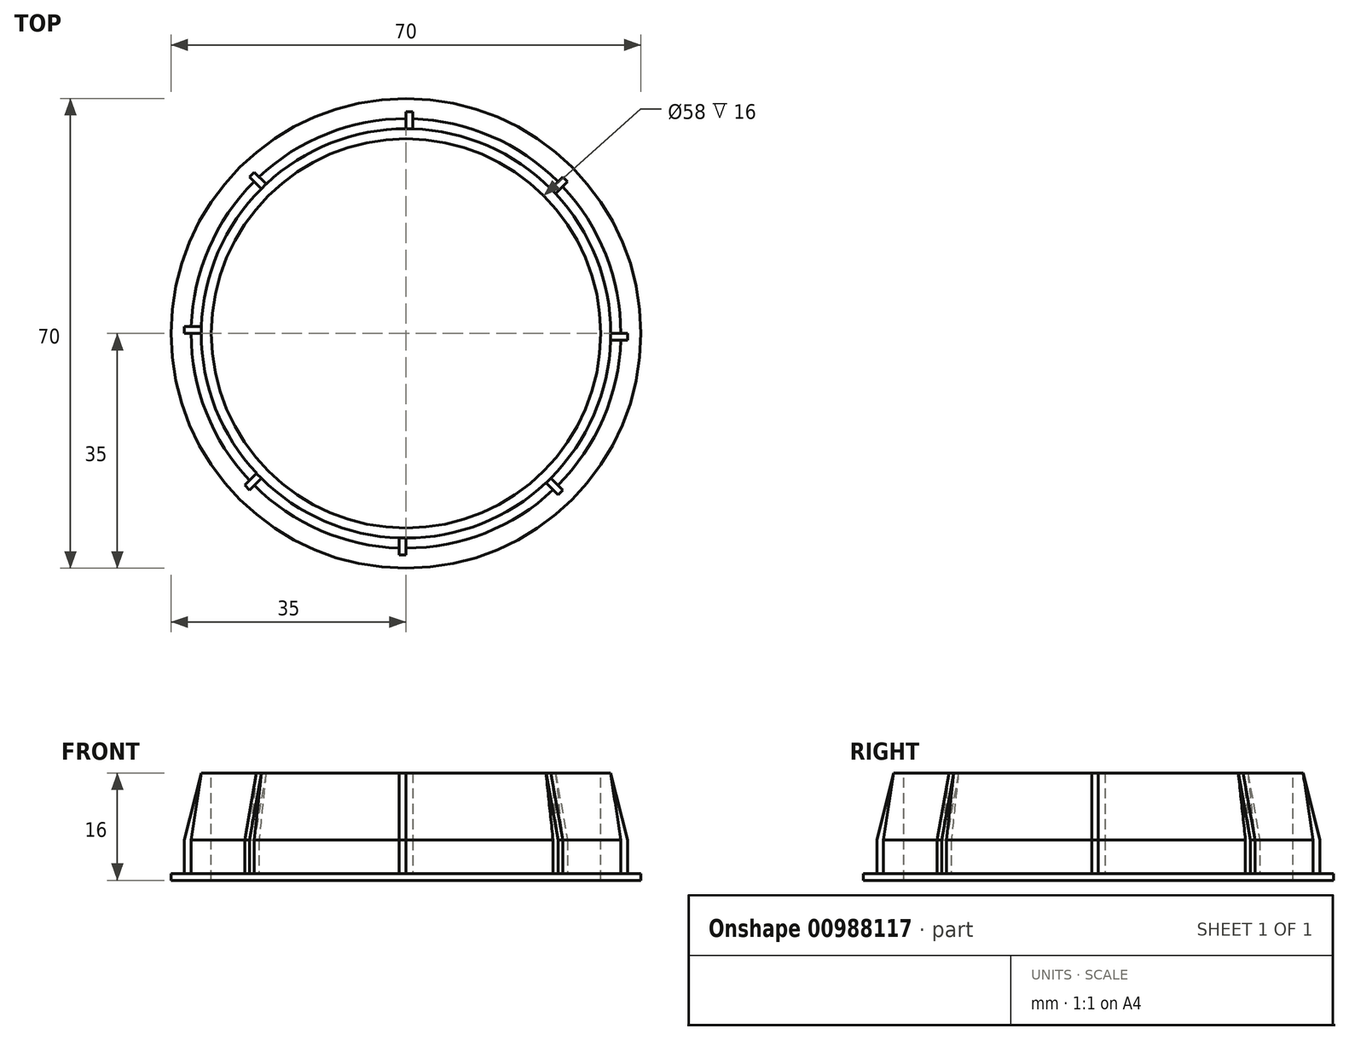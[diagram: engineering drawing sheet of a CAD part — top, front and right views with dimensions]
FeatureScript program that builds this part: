
annotation { "Feature Type Name" : "Feature", "Feature Type Description" : "" }
export const myFeature = defineFeature(function(context is Context, id is Id, definition is map)
    precondition{}
    {
        {
            var Q0;
            Q0=qCreatedBy(makeId("Top.planeOp"),FACE);
            var sketch = newSketch(context, id + "F0", { "sketchPlane" : qUnion([Q0])});
            skCircle(sketch, "E0", {"center": v(0, 0) * mm, "radius": 35 * mm});
            skSolve(sketch);
        }
        {
            var Q0;
            Q0 = qSketchRegion(id + "F0", true);
            extrude(context, id + "F1", {"entities" : qUnion([Q0]), "depth" : 1 * mm, "offsetDistance" : 25 * mm});
        }
        {
            var Q0;
            Q0=makeQuery(id+"F1.opExtrude","CAP_FACE",FACE,{"disambiguationData":[OSD([sQuery(id+"F0.wireOp",EDGE,"E0")])],"isStart":false});
            var sketch = newSketch(context, id + "F2", { "sketchPlane" : qUnion([Q0])});
            skCircle(sketch, "E1", {"center": v(0, 0) * mm, "radius": 32 * mm});
            skLineSegment(sketch, "E2.bottom", {"start": v(0, 32) * mm, "end": v(1, 32) * mm});
            skLineSegment(sketch, "E2.top", {"start": v(0, 33) * mm, "end": v(1, 33) * mm});
            skLineSegment(sketch, "E2.left", {"start": v(0, 32) * mm, "end": v(0, 33) * mm});
            skLineSegment(sketch, "E2.right", {"start": v(1, 32) * mm, "end": v(1, 33) * mm});
            skLineSegment(sketch, "E3.top", {"start": v(0, 31) * mm, "end": v(1, 31) * mm});
            skLineSegment(sketch, "E3.left", {"start": v(0, 32) * mm, "end": v(0, 31) * mm});
            skLineSegment(sketch, "E3.right", {"start": v(1, 32) * mm, "end": v(1, 31) * mm});
            skLineSegment(sketch, "E4.1.0", {"start": v(-22.63, 22.63) * mm, "end": v(-23.33, 23.33) * mm});
            skLineSegment(sketch, "E4.1.1", {"start": v(-21.92, 23.33) * mm, "end": v(-21.21, 22.63) * mm});
            skLineSegment(sketch, "E4.1.2", {"start": v(-22.63, 22.63) * mm, "end": v(-21.92, 21.92) * mm});
            skLineSegment(sketch, "E4.1.3", {"start": v(-23.33, 23.33) * mm, "end": v(-22.63, 24.04) * mm});
            skLineSegment(sketch, "E4.1.4", {"start": v(-21.92, 23.33) * mm, "end": v(-22.63, 24.04) * mm});
            skLineSegment(sketch, "E4.1.5", {"start": v(-22.63, 22.63) * mm, "end": v(-21.92, 23.33) * mm});
            skLineSegment(sketch, "E4.1.6", {"start": v(-21.92, 21.92) * mm, "end": v(-21.21, 22.63) * mm});
            skLineSegment(sketch, "E4.1.7", {"start": v(-22.63, 22.63) * mm, "end": v(-21.92, 23.33) * mm});
            skLineSegment(sketch, "E4.2.0", {"start": v(-32, 0) * mm, "end": v(-33, 0) * mm});
            skLineSegment(sketch, "E4.2.1", {"start": v(-32, 1) * mm, "end": v(-31, 1) * mm});
            skLineSegment(sketch, "E4.2.2", {"start": v(-32, 0) * mm, "end": v(-31, 0) * mm});
            skLineSegment(sketch, "E4.2.3", {"start": v(-33, 0) * mm, "end": v(-33, 1) * mm});
            skLineSegment(sketch, "E4.2.4", {"start": v(-32, 1) * mm, "end": v(-33, 1) * mm});
            skLineSegment(sketch, "E4.2.5", {"start": v(-32, 0) * mm, "end": v(-32, 1) * mm});
            skLineSegment(sketch, "E4.2.6", {"start": v(-31, 0) * mm, "end": v(-31, 1) * mm});
            skLineSegment(sketch, "E4.2.7", {"start": v(-32, 0) * mm, "end": v(-32, 1) * mm});
            skLineSegment(sketch, "E4.3.0", {"start": v(-22.63, -22.63) * mm, "end": v(-23.33, -23.33) * mm});
            skLineSegment(sketch, "E4.3.1", {"start": v(-23.33, -21.92) * mm, "end": v(-22.63, -21.21) * mm});
            skLineSegment(sketch, "E4.3.2", {"start": v(-22.63, -22.63) * mm, "end": v(-21.92, -21.92) * mm});
            skLineSegment(sketch, "E4.3.3", {"start": v(-23.33, -23.33) * mm, "end": v(-24.04, -22.63) * mm});
            skLineSegment(sketch, "E4.3.4", {"start": v(-23.33, -21.92) * mm, "end": v(-24.04, -22.63) * mm});
            skLineSegment(sketch, "E4.3.5", {"start": v(-22.63, -22.63) * mm, "end": v(-23.33, -21.92) * mm});
            skLineSegment(sketch, "E4.3.6", {"start": v(-21.92, -21.92) * mm, "end": v(-22.63, -21.21) * mm});
            skLineSegment(sketch, "E4.3.7", {"start": v(-22.63, -22.63) * mm, "end": v(-23.33, -21.92) * mm});
            skLineSegment(sketch, "E4.4.0", {"start": v(0, -32) * mm, "end": v(0, -33) * mm});
            skLineSegment(sketch, "E4.4.1", {"start": v(-1, -32) * mm, "end": v(-1, -31) * mm});
            skLineSegment(sketch, "E4.4.2", {"start": v(0, -32) * mm, "end": v(0, -31) * mm});
            skLineSegment(sketch, "E4.4.3", {"start": v(0, -33) * mm, "end": v(-1, -33) * mm});
            skLineSegment(sketch, "E4.4.4", {"start": v(-1, -32) * mm, "end": v(-1, -33) * mm});
            skLineSegment(sketch, "E4.4.5", {"start": v(0, -32) * mm, "end": v(-1, -32) * mm});
            skLineSegment(sketch, "E4.4.6", {"start": v(0, -31) * mm, "end": v(-1, -31) * mm});
            skLineSegment(sketch, "E4.4.7", {"start": v(0, -32) * mm, "end": v(-1, -32) * mm});
            skLineSegment(sketch, "E4.5.0", {"start": v(22.63, -22.63) * mm, "end": v(23.33, -23.33) * mm});
            skLineSegment(sketch, "E4.5.1", {"start": v(21.92, -23.33) * mm, "end": v(21.21, -22.63) * mm});
            skLineSegment(sketch, "E4.5.2", {"start": v(22.63, -22.63) * mm, "end": v(21.92, -21.92) * mm});
            skLineSegment(sketch, "E4.5.3", {"start": v(23.33, -23.33) * mm, "end": v(22.63, -24.04) * mm});
            skLineSegment(sketch, "E4.5.4", {"start": v(21.92, -23.33) * mm, "end": v(22.63, -24.04) * mm});
            skLineSegment(sketch, "E4.5.5", {"start": v(22.63, -22.63) * mm, "end": v(21.92, -23.33) * mm});
            skLineSegment(sketch, "E4.5.6", {"start": v(21.92, -21.92) * mm, "end": v(21.21, -22.63) * mm});
            skLineSegment(sketch, "E4.5.7", {"start": v(22.63, -22.63) * mm, "end": v(21.92, -23.33) * mm});
            skLineSegment(sketch, "E4.6.0", {"start": v(32, 0) * mm, "end": v(33, 0) * mm});
            skLineSegment(sketch, "E4.6.1", {"start": v(32, -1) * mm, "end": v(31, -1) * mm});
            skLineSegment(sketch, "E4.6.2", {"start": v(32, 0) * mm, "end": v(31, 0) * mm});
            skLineSegment(sketch, "E4.6.3", {"start": v(33, 0) * mm, "end": v(33, -1) * mm});
            skLineSegment(sketch, "E4.6.4", {"start": v(32, -1) * mm, "end": v(33, -1) * mm});
            skLineSegment(sketch, "E4.6.5", {"start": v(32, 0) * mm, "end": v(32, -1) * mm});
            skLineSegment(sketch, "E4.6.6", {"start": v(31, 0) * mm, "end": v(31, -1) * mm});
            skLineSegment(sketch, "E4.6.7", {"start": v(32, 0) * mm, "end": v(32, -1) * mm});
            skLineSegment(sketch, "E4.7.0", {"start": v(22.63, 22.63) * mm, "end": v(23.33, 23.33) * mm});
            skLineSegment(sketch, "E4.7.1", {"start": v(23.33, 21.92) * mm, "end": v(22.63, 21.21) * mm});
            skLineSegment(sketch, "E4.7.2", {"start": v(22.63, 22.63) * mm, "end": v(21.92, 21.92) * mm});
            skLineSegment(sketch, "E4.7.3", {"start": v(23.33, 23.33) * mm, "end": v(24.04, 22.63) * mm});
            skLineSegment(sketch, "E4.7.4", {"start": v(23.33, 21.92) * mm, "end": v(24.04, 22.63) * mm});
            skLineSegment(sketch, "E4.7.5", {"start": v(22.63, 22.63) * mm, "end": v(23.33, 21.92) * mm});
            skLineSegment(sketch, "E4.7.6", {"start": v(21.92, 21.92) * mm, "end": v(22.63, 21.21) * mm});
            skLineSegment(sketch, "E4.7.7", {"start": v(22.63, 22.63) * mm, "end": v(23.33, 21.92) * mm});
            skSolve(sketch);
        }
        {
            var Q0;
            Q0 = qSketchRegion(id + "F2", true);
            extrude(context, id + "F3", {"entities" : qUnion([Q0]), "operationType" : NewBodyOperationType.ADD, "depth" : 15 * mm, "offsetDistance" : 25 * mm});
        }
        {
            var Q0;
            Q0=makeQuery(id+"F3.opExtrude","CAP_FACE",FACE,{"disambiguationData":[OSD([sQuery(id+"F2.wireOp",EDGE,"E1"),sQuery(id+"F2.wireOp",EDGE,"E2.top"),sQuery(id+"F2.wireOp",EDGE,"E2.left"),sQuery(id+"F2.wireOp",EDGE,"E2.right"),sQuery(id+"F2.wireOp",EDGE,"E3.right"),sQuery(id+"F2.wireOp",EDGE,"E4.1.0"),sQuery(id+"F2.wireOp",EDGE,"E4.1.1"),sQuery(id+"F2.wireOp",EDGE,"E4.1.3"),sQuery(id+"F2.wireOp",EDGE,"E4.1.4"),sQuery(id+"F2.wireOp",EDGE,"E4.2.0"),sQuery(id+"F2.wireOp",EDGE,"E4.2.1"),sQuery(id+"F2.wireOp",EDGE,"E4.2.3"),sQuery(id+"F2.wireOp",EDGE,"E4.2.4"),sQuery(id+"F2.wireOp",EDGE,"E4.3.0"),sQuery(id+"F2.wireOp",EDGE,"E4.3.1"),sQuery(id+"F2.wireOp",EDGE,"E4.3.3"),sQuery(id+"F2.wireOp",EDGE,"E4.3.4"),sQuery(id+"F2.wireOp",EDGE,"E4.4.0"),sQuery(id+"F2.wireOp",EDGE,"E4.4.1"),sQuery(id+"F2.wireOp",EDGE,"E4.4.3"),sQuery(id+"F2.wireOp",EDGE,"E4.4.4"),sQuery(id+"F2.wireOp",EDGE,"E4.5.0"),sQuery(id+"F2.wireOp",EDGE,"E4.5.1"),sQuery(id+"F2.wireOp",EDGE,"E4.5.3"),sQuery(id+"F2.wireOp",EDGE,"E4.5.4"),sQuery(id+"F2.wireOp",EDGE,"E4.6.0"),sQuery(id+"F2.wireOp",EDGE,"E4.6.1"),sQuery(id+"F2.wireOp",EDGE,"E4.6.3"),sQuery(id+"F2.wireOp",EDGE,"E4.6.4"),sQuery(id+"F2.wireOp",EDGE,"E4.7.0"),sQuery(id+"F2.wireOp",EDGE,"E4.7.1"),sQuery(id+"F2.wireOp",EDGE,"E4.7.3"),sQuery(id+"F2.wireOp",EDGE,"E4.7.4")])],"isStart":false});
            var sketch = newSketch(context, id + "F4", { "sketchPlane" : qUnion([Q0])});
            skCircle(sketch, "E5", {"center": v(0, 0) * mm, "radius": 29 * mm});
            skSolve(sketch);
        }
        {
            var Q0;
            Q0 = qSketchRegion(id + "F4", true);
            extrude(context, id + "F5", {"entities" : qUnion([Q0]), "operationType" : NewBodyOperationType.REMOVE, "endBound" : BoundingType.THROUGH_ALL, "oppositeDirection" : true, "depth" : 25 * mm, "offsetDistance" : 25 * mm});
        }
        {
            var Q0;
            {var subQ0=sQuery(id+"F2.wireOp",EDGE,"E1");Q0=makeQuery(id+"F3.opExtrude","CAP_EDGE",EDGE,{"disambiguationData":[OSD([subQ0]),TDD([makeQuery(id+"F2.imprint","IMPRINT",EDGE,{"disambiguationData":[TD([[makeQuery(id+"F2.imprint","INTERSECT",VERTEX,{"derivedFrom":[subQ0,sQuery(id+"F2.wireOp",EDGE,"E3.right")]}),1.0]])],"derivedFrom":subQ0})])],"isStart":false});}
            var Q1;
            {var subQ0=sQuery(id+"F2.wireOp",EDGE,"E1");Q1=makeQuery(id+"F3.opExtrude","CAP_EDGE",EDGE,{"disambiguationData":[OSD([subQ0]),TDD([makeQuery(id+"F2.imprint","IMPRINT",EDGE,{"disambiguationData":[TD([[makeQuery(id+"F2.imprint","INTERSECT",VERTEX,{"derivedFrom":[subQ0,sQuery(id+"F2.wireOp",EDGE,"E4.7.1")]}),1.0]])],"derivedFrom":subQ0})])],"isStart":false});}
            var Q2;
            {var subQ0=sQuery(id+"F2.wireOp",EDGE,"E1");Q2=makeQuery(id+"F3.opExtrude","CAP_EDGE",EDGE,{"disambiguationData":[OSD([subQ0]),TDD([makeQuery(id+"F2.imprint","IMPRINT",EDGE,{"disambiguationData":[TD([[makeQuery(id+"F2.imprint","INTERSECT",VERTEX,{"derivedFrom":[subQ0,sQuery(id+"F2.wireOp",EDGE,"E4.6.1")]}),1.0]])],"derivedFrom":subQ0})])],"isStart":false});}
            var Q3;
            {var subQ0=sQuery(id+"F2.wireOp",EDGE,"E1");Q3=makeQuery(id+"F3.opExtrude","CAP_EDGE",EDGE,{"disambiguationData":[OSD([subQ0]),TDD([makeQuery(id+"F2.imprint","IMPRINT",EDGE,{"disambiguationData":[TD([[makeQuery(id+"F2.imprint","INTERSECT",VERTEX,{"derivedFrom":[subQ0,sQuery(id+"F2.wireOp",EDGE,"E4.5.1")]}),1.0]])],"derivedFrom":subQ0})])],"isStart":false});}
            var Q4;
            {var subQ0=sQuery(id+"F2.wireOp",EDGE,"E1");Q4=makeQuery(id+"F3.opExtrude","CAP_EDGE",EDGE,{"disambiguationData":[OSD([subQ0]),TDD([makeQuery(id+"F2.imprint","IMPRINT",EDGE,{"disambiguationData":[TD([[makeQuery(id+"F2.imprint","INTERSECT",VERTEX,{"derivedFrom":[subQ0,sQuery(id+"F2.wireOp",EDGE,"E4.4.1")]}),1.0]])],"derivedFrom":subQ0})])],"isStart":false});}
            var Q5;
            {var subQ0=sQuery(id+"F2.wireOp",EDGE,"E1");Q5=makeQuery(id+"F3.opExtrude","CAP_EDGE",EDGE,{"disambiguationData":[OSD([subQ0]),TDD([makeQuery(id+"F2.imprint","IMPRINT",EDGE,{"disambiguationData":[TD([[makeQuery(id+"F2.imprint","INTERSECT",VERTEX,{"derivedFrom":[subQ0,sQuery(id+"F2.wireOp",EDGE,"E4.3.1")]}),1.0]])],"derivedFrom":subQ0})])],"isStart":false});}
            var Q6;
            {var subQ0=sQuery(id+"F2.wireOp",EDGE,"E1");Q6=makeQuery(id+"F3.opExtrude","CAP_EDGE",EDGE,{"disambiguationData":[OSD([subQ0]),TDD([makeQuery(id+"F2.imprint","IMPRINT",EDGE,{"disambiguationData":[TD([[makeQuery(id+"F2.imprint","INTERSECT",VERTEX,{"derivedFrom":[subQ0,sQuery(id+"F2.wireOp",EDGE,"E4.2.1")]}),1.0]])],"derivedFrom":subQ0})])],"isStart":false});}
            var Q7;
            {var subQ0=sQuery(id+"F2.wireOp",EDGE,"E1");Q7=makeQuery(id+"F3.opExtrude","CAP_EDGE",EDGE,{"disambiguationData":[OSD([subQ0]),TDD([makeQuery(id+"F2.imprint","IMPRINT",EDGE,{"disambiguationData":[TD([[makeQuery(id+"F2.imprint","INTERSECT",VERTEX,{"derivedFrom":[subQ0,sQuery(id+"F2.wireOp",EDGE,"E4.1.1")]}),1.0]])],"derivedFrom":subQ0})])],"isStart":false});}
            chamfer(context, id + "F6", {"entities" : qUnion([Q0, Q1, Q2, Q3, Q4, Q5, Q6, Q7]), "chamferType" : ChamferType.TWO_OFFSETS, "width1" : 1.5 * mm, "oppositeDirection" : false, "width2" : 10 * mm, "tangentPropagation" : true});
        }
        {
            var Q0;
            Q0=makeQuery(id+"F3.opExtrude","CAP_EDGE",EDGE,{"disambiguationData":[OSD([sQuery(id+"F2.wireOp",EDGE,"E4.6.3")])],"isStart":false});
            var Q1;
            Q1=makeQuery(id+"F3.opExtrude","CAP_EDGE",EDGE,{"disambiguationData":[OSD([sQuery(id+"F2.wireOp",EDGE,"E4.5.3")])],"isStart":false});
            var Q2;
            Q2=makeQuery(id+"F3.opExtrude","CAP_EDGE",EDGE,{"disambiguationData":[OSD([sQuery(id+"F2.wireOp",EDGE,"E4.4.3")])],"isStart":false});
            var Q3;
            Q3=makeQuery(id+"F3.opExtrude","CAP_EDGE",EDGE,{"disambiguationData":[OSD([sQuery(id+"F2.wireOp",EDGE,"E4.3.3")])],"isStart":false});
            var Q4;
            Q4=makeQuery(id+"F3.opExtrude","CAP_EDGE",EDGE,{"disambiguationData":[OSD([sQuery(id+"F2.wireOp",EDGE,"E4.2.3")])],"isStart":false});
            var Q5;
            Q5=makeQuery(id+"F3.opExtrude","CAP_EDGE",EDGE,{"disambiguationData":[OSD([sQuery(id+"F2.wireOp",EDGE,"E4.1.3")])],"isStart":false});
            var Q6;
            Q6=makeQuery(id+"F3.opExtrude","CAP_EDGE",EDGE,{"disambiguationData":[OSD([sQuery(id+"F2.wireOp",EDGE,"E2.top")])],"isStart":false});
            var Q7;
            Q7=makeQuery(id+"F3.opExtrude","CAP_EDGE",EDGE,{"disambiguationData":[OSD([sQuery(id+"F2.wireOp",EDGE,"E4.7.3")])],"isStart":false});
            chamfer(context, id + "F7", {"entities" : qUnion([Q0, Q1, Q2, Q3, Q4, Q5, Q6, Q7]), "chamferType" : ChamferType.TWO_OFFSETS, "width1" : 10 * mm, "oppositeDirection" : false, "width2" : 2.5 * mm, "tangentPropagation" : true});
        }
    });
